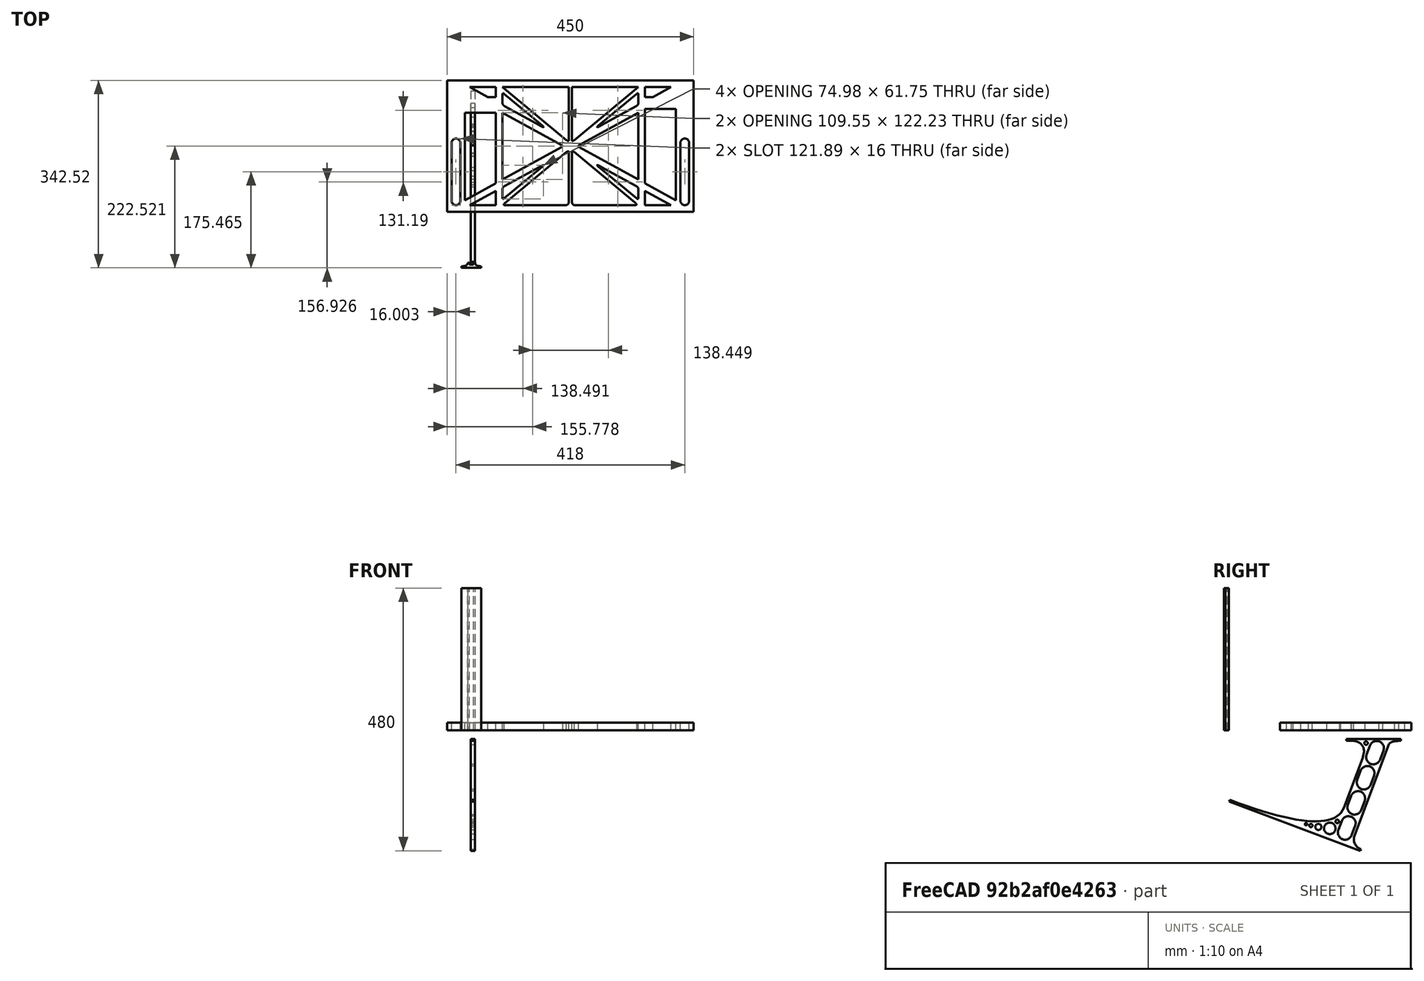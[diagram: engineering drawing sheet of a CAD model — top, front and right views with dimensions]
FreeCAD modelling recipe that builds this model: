
FCSTD DOCUMENT  (FreeCAD 0.19R0.19.2)
Label: laptopStand082
License: All rights reserved
LicenseURL: http://en.wikipedia.org/wiki/All_rights_reserved
objects: Sketcher::SketchObject×3, Part::Extrusion×3
note: 6 computed .brp shape members not serialized (recipe doc carries the construction recipe); baked Part::Feature solids carry a one-line shape summary decoded from their .brp

FEATURE [Sketcher::SketchObject] Sketch
  FullyConstrained = false
  sketch-geometry (204):
    g0: LineSegment StartX=-10.9272 StartY=-82.7794 StartZ=0 EndX=46.0728 EndY=-51.4823 EndZ=0
    g1: LineSegment StartX=366.073 StartY=-91.7794 StartZ=0 EndX=318.073 EndY=-65.424 EndZ=0
    g2: LineSegment StartX=-10.9272 StartY=77.3346 StartZ=0 EndX=-10.9272 EndY=-82.7794 EndZ=0
    g3: LineSegment StartX=375.073 StartY=-82.7794 StartZ=0 EndX=375.073 EndY=83.9235 EndZ=0
    g4: LineSegment StartX=-1.92719 StartY=-91.7794 StartZ=0 EndX=46.0728 EndY=-91.7794 EndZ=0
    g5: LineSegment StartX=318.073 StartY=124.221 StartZ=0 EndX=366.073 EndY=124.221 EndZ=0
    g6: LineSegment StartX=306.073 StartY=124.221 StartZ=0 EndX=189.124 EndY=27.0628 EndZ=0
    g7: LineSegment StartX=175.022 StartY=27.0628 StartZ=0 EndX=58.0728 EndY=124.221 EndZ=0
    g8: LineSegment StartX=306.073 StartY=77.3346 StartZ=0 EndX=306.073 EndY=-44.8935 EndZ=0
    g9: LineSegment StartX=318.073 StartY=83.9235 StartZ=0 EndX=318.073 EndY=-51.4823 EndZ=0
    g10: LineSegment StartX=318.073 StartY=-51.4823 StartZ=0 EndX=375.073 EndY=-82.7794 EndZ=0
    g11: LineSegment StartX=318.073 StartY=-65.424 StartZ=0 EndX=318.073 EndY=-91.7794 EndZ=0
    g12: LineSegment StartX=318.073 StartY=-91.7794 StartZ=0 EndX=366.073 EndY=-91.7794 EndZ=0
    g13: LineSegment StartX=58.0728 StartY=-44.8935 StartZ=0 EndX=58.0728 EndY=77.3346 EndZ=0
    g14: LineSegment StartX=46.0728 StartY=-65.424 StartZ=0 EndX=-1.92719 EndY=-91.7794 EndZ=0
    g15: LineSegment StartX=46.0728 StartY=-65.424 StartZ=0 EndX=46.0728 EndY=-91.7794 EndZ=0
    g16: LineSegment StartX=46.0728 StartY=77.3346 StartZ=0 EndX=46.0728 EndY=-51.4823 EndZ=0
    g17: LineSegment StartX=-42.9272 StartY=136.221 StartZ=0 EndX=-42.9272 EndY=-103.779 EndZ=0
    g18: LineSegment StartX=407.073 StartY=136.221 StartZ=0 EndX=407.073 EndY=-103.779 EndZ=0
    g19: LineSegment StartX=179.022 StartY=27.0628 StartZ=0 EndX=179.022 EndY=124.221 EndZ=0
    g20: LineSegment StartX=185.124 StartY=27.0628 StartZ=0 EndX=185.124 EndY=124.221 EndZ=0
    g21: ArcOfCircle CenterX=-26.9272 CenterY=22.1087 CenterZ=0 NormalX=0 NormalY=0 NormalZ=1 AngleXU=0 Radius=8 StartAngle=1e-16 EndAngle=3.14159
    g22: ArcOfCircle CenterX=-26.9272 CenterY=-83.7794 CenterZ=0 NormalX=0 NormalY=0 NormalZ=1 AngleXU=0 Radius=8 StartAngle=3.14159 EndAngle=6.28319
    g23: LineSegment StartX=-34.9272 StartY=22.1087 StartZ=0 EndX=-34.9272 EndY=-83.7794 EndZ=0
    g24: LineSegment StartX=-18.9272 StartY=22.1087 StartZ=0 EndX=-18.9272 EndY=-83.7794 EndZ=0
    g25: LineSegment StartX=306.073 StartY=124.221 StartZ=0 EndX=185.124 EndY=124.221 EndZ=0
    g26: LineSegment StartX=179.022 StartY=124.221 StartZ=0 EndX=58.0728 EndY=124.221 EndZ=0
    g27: ArcOfCircle CenterX=391.073 CenterY=22.1087 CenterZ=0 NormalX=0 NormalY=0 NormalZ=1 AngleXU=0 Radius=8 StartAngle=-4.4e-15 EndAngle=3.14159
    g28: LineSegment StartX=399.073 StartY=22.1087 StartZ=0 EndX=399.073 EndY=-83.7794 EndZ=0
    g29: LineSegment StartX=383.073 StartY=22.1087 StartZ=0 EndX=383.073 EndY=-83.7794 EndZ=0
    g30: ArcOfCircle CenterX=391.073 CenterY=-83.7794 CenterZ=0 NormalX=0 NormalY=0 NormalZ=1 AngleXU=0 Radius=8 StartAngle=3.14159 EndAngle=6.28319
    g31: Circle CenterX=175.022 CenterY=27.0628 CenterZ=0 NormalX=0 NormalY=0 NormalZ=1 AngleXU=0 Radius=1
    g32: Circle CenterX=179.022 CenterY=24.8665 CenterZ=0 NormalX=0 NormalY=0 NormalZ=1 AngleXU=0 Radius=1
    g33: Circle CenterX=179.022 CenterY=27.0628 CenterZ=0 NormalX=0 NormalY=0 NormalZ=1 AngleXU=0 Radius=1
    g34: BSplineCurve PolesCount=3 KnotsCount=2 Degree=2 IsPeriodic=0
    g35: GeomPoint X=175.022 Y=27.0628 Z=0
    g36: GeomPoint X=179.022 Y=27.0628 Z=0
    g37: Circle CenterX=189.124 CenterY=27.0628 CenterZ=0 NormalX=0 NormalY=0 NormalZ=1 AngleXU=0 Radius=1
    g38: Circle CenterX=185.124 CenterY=24.8665 CenterZ=0 NormalX=0 NormalY=0 NormalZ=1 AngleXU=0 Radius=1
    g39: Circle CenterX=185.124 CenterY=27.0628 CenterZ=0 NormalX=0 NormalY=0 NormalZ=1 AngleXU=0 Radius=1
    g40: BSplineCurve PolesCount=3 KnotsCount=2 Degree=2 IsPeriodic=0
    g41: GeomPoint X=189.124 Y=27.0628 Z=0
    g42: GeomPoint X=185.124 Y=27.0628 Z=0
    g43: Circle CenterX=175.022 CenterY=5.37834 CenterZ=0 NormalX=0 NormalY=0 NormalZ=1 AngleXU=0 Radius=1
    g44: Circle CenterX=179.022 CenterY=7.57463 CenterZ=0 NormalX=0 NormalY=0 NormalZ=1 AngleXU=0 Radius=1
    g45: Circle CenterX=179.022 CenterY=5.34704 CenterZ=0 NormalX=0 NormalY=0 NormalZ=1 AngleXU=0 Radius=1
    g46: BSplineCurve PolesCount=3 KnotsCount=2 Degree=2 IsPeriodic=0
    g47: GeomPoint X=175.022 Y=5.37834 Z=0
    g48: GeomPoint X=179.022 Y=5.34704 Z=0
    g49: Circle CenterX=189.124 CenterY=5.37834 CenterZ=0 NormalX=0 NormalY=0 NormalZ=1 AngleXU=0 Radius=1
    g50: Circle CenterX=185.124 CenterY=7.57463 CenterZ=0 NormalX=0 NormalY=0 NormalZ=1 AngleXU=0 Radius=1
    g51: Circle CenterX=185.124 CenterY=5.34704 CenterZ=0 NormalX=0 NormalY=0 NormalZ=1 AngleXU=0 Radius=1
    g52: BSplineCurve PolesCount=3 KnotsCount=2 Degree=2 IsPeriodic=0
    g53: GeomPoint X=189.124 Y=5.37834 Z=0
    g54: GeomPoint X=185.124 Y=5.34704 Z=0
    g55: Circle CenterX=165.871 CenterY=18.1458 CenterZ=0 NormalX=0 NormalY=0 NormalZ=1 AngleXU=0 Radius=1
    g56: Circle CenterX=169.377 CenterY=16.2206 CenterZ=0 NormalX=0 NormalY=0 NormalZ=1 AngleXU=0 Radius=1
    g57: Circle CenterX=165.871 CenterY=14.2954 CenterZ=0 NormalX=0 NormalY=0 NormalZ=1 AngleXU=0 Radius=1
    g58: BSplineCurve PolesCount=3 KnotsCount=2 Degree=2 IsPeriodic=0
    g59: GeomPoint X=165.871 Y=18.1458 Z=0
    g60: GeomPoint X=165.871 Y=14.2954 Z=0
    g61: Circle CenterX=198.275 CenterY=18.1458 CenterZ=0 NormalX=0 NormalY=0 NormalZ=1 AngleXU=0 Radius=1
    g62: Circle CenterX=194.768 CenterY=16.2206 CenterZ=0 NormalX=0 NormalY=0 NormalZ=1 AngleXU=0 Radius=1
    g63: Circle CenterX=198.275 CenterY=14.2954 CenterZ=0 NormalX=0 NormalY=0 NormalZ=1 AngleXU=0 Radius=1
    g64: BSplineCurve PolesCount=3 KnotsCount=2 Degree=2 IsPeriodic=0
    g65: GeomPoint X=198.275 Y=18.1458 Z=0
    g66: GeomPoint X=198.275 Y=14.2954 Z=0
    g67: LineSegment StartX=165.871 StartY=18.1458 StartZ=0 EndX=58.0728 EndY=77.3346 EndZ=0
    g68: LineSegment StartX=58.0728 StartY=-44.8935 StartZ=0 EndX=165.871 EndY=14.2954 EndZ=0
    g69: LineSegment StartX=198.275 StartY=18.1458 StartZ=0 EndX=306.073 EndY=77.3346 EndZ=0
    g70: LineSegment StartX=198.275 StartY=14.2954 StartZ=0 EndX=306.073 EndY=-44.8935 EndZ=0
    g71: LineSegment StartX=407.073 StartY=-103.779 StartZ=0 EndX=-42.9272 EndY=-103.779 EndZ=0
    g72: LineSegment StartX=407.073 StartY=136.221 StartZ=0 EndX=-42.9272 EndY=136.221 EndZ=0
    g73: LineSegment StartX=46.0728 StartY=77.3346 StartZ=0 EndX=-10.9272 EndY=77.3346 EndZ=0
    g74: LineSegment StartX=46.0728 StartY=105.865 StartZ=0 EndX=31.5028 EndY=105.865 EndZ=0
    g75: LineSegment StartX=46.0728 StartY=124.221 StartZ=0 EndX=46.0728 EndY=105.865 EndZ=0
    g76: LineSegment StartX=-1.92719 StartY=124.221 StartZ=0 EndX=31.5028 EndY=105.865 EndZ=0
    g77: LineSegment StartX=46.0728 StartY=124.221 StartZ=0 EndX=-1.92719 EndY=124.221 EndZ=0
    g78: LineSegment StartX=318.073 StartY=83.9235 StartZ=0 EndX=375.073 EndY=83.9235 EndZ=0
    g79: LineSegment StartX=318.073 StartY=105.865 StartZ=0 EndX=332.643 EndY=105.865 EndZ=0
    g80: LineSegment StartX=332.643 StartY=105.865 StartZ=0 EndX=366.073 EndY=124.221 EndZ=0
    g81: LineSegment StartX=318.073 StartY=124.221 StartZ=0 EndX=318.073 EndY=105.865 EndZ=0
    g82: Circle CenterX=125.607 CenterY=54.1951 CenterZ=0 NormalX=0 NormalY=0 NormalZ=1 AngleXU=0 Radius=1
    g83: Circle CenterX=139.632 CenterY=46.4944 CenterZ=0 NormalX=0 NormalY=0 NormalZ=1 AngleXU=0 Radius=1
    g84: Circle CenterX=127.326 CenterY=56.7187 CenterZ=0 NormalX=0 NormalY=0 NormalZ=1 AngleXU=0 Radius=1
    g85: BSplineCurve PolesCount=3 KnotsCount=2 Degree=2 IsPeriodic=0
    g86: GeomPoint X=125.607 Y=54.1951 Z=0
    g87: GeomPoint X=127.326 Y=56.7187 Z=0
    g88: Circle CenterX=236.821 CenterY=56.7187 CenterZ=0 NormalX=0 NormalY=0 NormalZ=1 AngleXU=0 Radius=1
    g89: Circle CenterX=224.513 CenterY=46.4944 CenterZ=0 NormalX=0 NormalY=0 NormalZ=1 AngleXU=0 Radius=1
    g90: Circle CenterX=238.538 CenterY=54.1951 CenterZ=0 NormalX=0 NormalY=0 NormalZ=1 AngleXU=0 Radius=1
    g91: BSplineCurve PolesCount=3 KnotsCount=2 Degree=2 IsPeriodic=0
    g92: GeomPoint X=236.821 Y=56.7187 Z=0
    g93: GeomPoint X=238.538 Y=54.1951 Z=0
    g94: Circle CenterX=238.538 CenterY=-21.7539 CenterZ=0 NormalX=0 NormalY=0 NormalZ=1 AngleXU=0 Radius=1
    g95: Circle CenterX=224.513 CenterY=-14.0532 CenterZ=0 NormalX=0 NormalY=0 NormalZ=1 AngleXU=0 Radius=1
    g96: Circle CenterX=236.821 CenterY=-24.2775 CenterZ=0 NormalX=0 NormalY=0 NormalZ=1 AngleXU=0 Radius=1
    g97: BSplineCurve PolesCount=3 KnotsCount=2 Degree=2 IsPeriodic=0
    g98: GeomPoint X=238.538 Y=-21.7539 Z=0
    g99: GeomPoint X=236.821 Y=-24.2775 Z=0
    g100: Circle CenterX=125.607 CenterY=-21.7539 CenterZ=0 NormalX=0 NormalY=0 NormalZ=1 AngleXU=0 Radius=1
    g101: Circle CenterX=139.632 CenterY=-14.0532 CenterZ=0 NormalX=0 NormalY=0 NormalZ=1 AngleXU=0 Radius=1
    g102: Circle CenterX=127.325 CenterY=-24.2775 CenterZ=0 NormalX=0 NormalY=0 NormalZ=1 AngleXU=0 Radius=1
    g103: BSplineCurve PolesCount=3 KnotsCount=2 Degree=2 IsPeriodic=0
    g104: GeomPoint X=125.607 Y=-21.7539 Z=0
    g105: GeomPoint X=127.325 Y=-24.2775 Z=0
    g106: Circle CenterX=302.996 CenterY=111.695 CenterZ=0 NormalX=0 NormalY=0 NormalZ=1 AngleXU=0 Radius=1
    g107: Circle CenterX=306.073 CenterY=114.251 CenterZ=0 NormalX=0 NormalY=0 NormalZ=1 AngleXU=0 Radius=1
    g108: Circle CenterX=306.073 CenterY=110.251 CenterZ=0 NormalX=0 NormalY=0 NormalZ=1 AngleXU=0 Radius=1
    g109: BSplineCurve PolesCount=3 KnotsCount=2 Degree=2 IsPeriodic=0
    g110: GeomPoint X=302.996 Y=111.695 Z=0
    g111: GeomPoint X=306.073 Y=110.251 Z=0
    g112: Circle CenterX=306.073 CenterY=95.2763 CenterZ=0 NormalX=0 NormalY=0 NormalZ=1 AngleXU=0 Radius=1
    g113: Circle CenterX=306.073 CenterY=91.2763 CenterZ=0 NormalX=0 NormalY=0 NormalZ=1 AngleXU=0 Radius=1
    g114: Circle CenterX=302.567 CenterY=89.3511 CenterZ=0 NormalX=0 NormalY=0 NormalZ=1 AngleXU=0 Radius=1
    g115: BSplineCurve PolesCount=3 KnotsCount=2 Degree=2 IsPeriodic=0
    g116: GeomPoint X=306.073 Y=95.2763 Z=0
    g117: GeomPoint X=302.567 Y=89.3511 Z=0
    g118: LineSegment StartX=306.073 StartY=110.251 StartZ=0 EndX=306.073 EndY=95.2763 EndZ=0
    g119: LineSegment StartX=302.996 StartY=111.695 StartZ=0 EndX=236.821 EndY=56.7187 EndZ=0
    g120: LineSegment StartX=238.538 StartY=54.1951 StartZ=0 EndX=302.567 EndY=89.3511 EndZ=0
    g121: Circle CenterX=61.1496 CenterY=111.695 CenterZ=0 NormalX=0 NormalY=0 NormalZ=1 AngleXU=0 Radius=1
    g122: Circle CenterX=58.0728 CenterY=114.251 CenterZ=0 NormalX=0 NormalY=0 NormalZ=1 AngleXU=0 Radius=1
    g123: Circle CenterX=58.0728 CenterY=110.251 CenterZ=0 NormalX=0 NormalY=0 NormalZ=1 AngleXU=0 Radius=1
    g124: BSplineCurve PolesCount=3 KnotsCount=2 Degree=2 IsPeriodic=0
    g125: GeomPoint X=61.1496 Y=111.695 Z=0
    g126: GeomPoint X=58.0728 Y=110.251 Z=0
    g127: Circle CenterX=61.5791 CenterY=89.3511 CenterZ=0 NormalX=0 NormalY=0 NormalZ=1 AngleXU=0 Radius=1
    g128: Circle CenterX=58.0728 CenterY=91.2763 CenterZ=0 NormalX=0 NormalY=0 NormalZ=1 AngleXU=0 Radius=1
    g129: Circle CenterX=58.0728 CenterY=95.2763 CenterZ=0 NormalX=0 NormalY=0 NormalZ=1 AngleXU=0 Radius=1
    g130: BSplineCurve PolesCount=3 KnotsCount=2 Degree=2 IsPeriodic=0
    g131: GeomPoint X=61.5791 Y=89.3511 Z=0
    g132: GeomPoint X=58.0728 Y=95.2763 Z=0
    g133: LineSegment StartX=58.0728 StartY=110.251 StartZ=0 EndX=58.0728 EndY=95.2763 EndZ=0
    g134: LineSegment StartX=61.1496 StartY=111.695 StartZ=0 EndX=127.326 EndY=56.7187 EndZ=0
    g135: LineSegment StartX=125.607 StartY=54.1951 StartZ=0 EndX=61.5791 EndY=89.3511 EndZ=0
    g136: Circle CenterX=61.5791 CenterY=-56.9099 CenterZ=0 NormalX=0 NormalY=0 NormalZ=1 AngleXU=0 Radius=1
    g137: Circle CenterX=58.0728 CenterY=-58.8351 CenterZ=0 NormalX=0 NormalY=0 NormalZ=1 AngleXU=0 Radius=1
    g138: Circle CenterX=58.0728 CenterY=-62.8351 CenterZ=0 NormalX=0 NormalY=0 NormalZ=1 AngleXU=0 Radius=1
    g139: BSplineCurve PolesCount=3 KnotsCount=2 Degree=2 IsPeriodic=0
    g140: GeomPoint X=61.5791 Y=-56.9099 Z=0
    g141: GeomPoint X=58.0728 Y=-62.8351 Z=0
    g142: Circle CenterX=58.0728 CenterY=-77.8102 CenterZ=0 NormalX=0 NormalY=0 NormalZ=1 AngleXU=0 Radius=1
    g143: Circle CenterX=58.0728 CenterY=-81.8102 CenterZ=0 NormalX=0 NormalY=0 NormalZ=1 AngleXU=0 Radius=1
    g144: Circle CenterX=61.1496 CenterY=-79.2541 CenterZ=0 NormalX=0 NormalY=0 NormalZ=1 AngleXU=0 Radius=1
    g145: BSplineCurve PolesCount=3 KnotsCount=2 Degree=2 IsPeriodic=0
    g146: GeomPoint X=58.0728 Y=-77.8102 Z=0
    g147: GeomPoint X=61.1496 Y=-79.2541 Z=0
    g148: LineSegment StartX=58.0728 StartY=-62.8351 StartZ=0 EndX=58.0728 EndY=-77.8102 EndZ=0
    g149: LineSegment StartX=61.1496 StartY=-79.2541 StartZ=0 EndX=127.325 EndY=-24.2775 EndZ=0
    g150: LineSegment StartX=125.607 StartY=-21.7539 StartZ=0 EndX=61.5791 EndY=-56.9099 EndZ=0
    g151: Circle CenterX=302.567 CenterY=-56.9099 CenterZ=0 NormalX=0 NormalY=0 NormalZ=1 AngleXU=0 Radius=1
    g152: Circle CenterX=306.073 CenterY=-58.8351 CenterZ=0 NormalX=0 NormalY=0 NormalZ=1 AngleXU=0 Radius=1
    g153: Circle CenterX=306.073 CenterY=-62.8351 CenterZ=0 NormalX=0 NormalY=0 NormalZ=1 AngleXU=0 Radius=1
    g154: BSplineCurve PolesCount=3 KnotsCount=2 Degree=2 IsPeriodic=0
    g155: GeomPoint X=302.567 Y=-56.9099 Z=0
    g156: GeomPoint X=306.073 Y=-62.8351 Z=0
    g157: Circle CenterX=302.996 CenterY=-79.2541 CenterZ=0 NormalX=0 NormalY=0 NormalZ=1 AngleXU=0 Radius=1
    g158: Circle CenterX=306.073 CenterY=-81.8102 CenterZ=0 NormalX=0 NormalY=0 NormalZ=1 AngleXU=0 Radius=1
    g159: Circle CenterX=306.073 CenterY=-77.8102 CenterZ=0 NormalX=0 NormalY=0 NormalZ=1 AngleXU=0 Radius=1
    g160: BSplineCurve PolesCount=3 KnotsCount=2 Degree=2 IsPeriodic=0
    g161: GeomPoint X=302.996 Y=-79.2541 Z=0
    g162: GeomPoint X=306.073 Y=-77.8102 Z=0
    g163: LineSegment StartX=306.073 StartY=-62.8351 StartZ=0 EndX=306.073 EndY=-77.8102 EndZ=0
    g164: LineSegment StartX=302.996 StartY=-79.2541 StartZ=0 EndX=236.821 EndY=-24.2775 EndZ=0
    g165: LineSegment StartX=238.538 StartY=-21.7539 StartZ=0 EndX=302.567 EndY=-56.9099 EndZ=0
    g166: Circle CenterX=61.6457 CenterY=-88.8112 CenterZ=0 NormalX=0 NormalY=0 NormalZ=1 AngleXU=0 Radius=1
    g167: Circle CenterX=58.0728 CenterY=-91.7794 CenterZ=0 NormalX=0 NormalY=0 NormalZ=1 AngleXU=0 Radius=1
    g168: Circle CenterX=63.9135 CenterY=-91.7794 CenterZ=0 NormalX=0 NormalY=0 NormalZ=1 AngleXU=0 Radius=1
    g169: BSplineCurve PolesCount=3 KnotsCount=2 Degree=2 IsPeriodic=0
    g170: GeomPoint X=61.6457 Y=-88.8112 Z=0
    g171: GeomPoint X=63.9135 Y=-91.7794 Z=0
    g172: Circle CenterX=179.022 CenterY=-85.8163 CenterZ=0 NormalX=0 NormalY=0 NormalZ=1 AngleXU=0 Radius=1
    g173: Circle CenterX=179.022 CenterY=-91.7794 CenterZ=0 NormalX=0 NormalY=0 NormalZ=1 AngleXU=0 Radius=1
    g174: Circle CenterX=171.895 CenterY=-91.7794 CenterZ=0 NormalX=0 NormalY=0 NormalZ=1 AngleXU=0 Radius=1
    g175: BSplineCurve PolesCount=3 KnotsCount=2 Degree=2 IsPeriodic=0
    g176: GeomPoint X=179.022 Y=-85.8163 Z=0
    g177: GeomPoint X=171.895 Y=-91.7794 Z=0
    g178: Circle CenterX=185.124 CenterY=-86.2028 CenterZ=0 NormalX=0 NormalY=0 NormalZ=1 AngleXU=0 Radius=1
    g179: Circle CenterX=185.124 CenterY=-91.7794 CenterZ=0 NormalX=0 NormalY=0 NormalZ=1 AngleXU=0 Radius=1
    g180: Circle CenterX=191.747 CenterY=-91.7794 CenterZ=0 NormalX=0 NormalY=0 NormalZ=1 AngleXU=0 Radius=1
    g181: BSplineCurve PolesCount=3 KnotsCount=2 Degree=2 IsPeriodic=0
    g182: GeomPoint X=185.124 Y=-86.2028 Z=0
    g183: GeomPoint X=191.747 Y=-91.7794 Z=0
    g184: Circle CenterX=299.888 CenterY=-86.6413 CenterZ=0 NormalX=0 NormalY=0 NormalZ=1 AngleXU=0 Radius=1
    g185: Circle CenterX=306.073 CenterY=-91.7794 CenterZ=0 NormalX=0 NormalY=0 NormalZ=1 AngleXU=0 Radius=1
    g186: Circle CenterX=298.776 CenterY=-91.7794 CenterZ=0 NormalX=0 NormalY=0 NormalZ=1 AngleXU=0 Radius=1
    g187: BSplineCurve PolesCount=3 KnotsCount=2 Degree=2 IsPeriodic=0
    g188: GeomPoint X=299.888 Y=-86.6413 Z=0
    g189: GeomPoint X=298.776 Y=-91.7794 Z=0
    g190: LineSegment StartX=189.124 StartY=5.37834 StartZ=0 EndX=299.888 EndY=-86.6413 EndZ=0
    g191: LineSegment StartX=298.776 StartY=-91.7794 StartZ=0 EndX=191.747 EndY=-91.7794 EndZ=0
    g192: LineSegment StartX=185.124 StartY=-86.2028 StartZ=0 EndX=185.124 EndY=5.34704 EndZ=0
    g193: LineSegment StartX=179.022 StartY=5.34704 StartZ=0 EndX=179.022 EndY=-85.8163 EndZ=0
    g194: LineSegment StartX=171.895 StartY=-91.7794 StartZ=0 EndX=63.9135 EndY=-91.7794 EndZ=0
    g195: LineSegment StartX=61.6457 StartY=-88.8112 StartZ=0 EndX=175.022 EndY=5.37834 EndZ=0
    g196: LineSegment StartX=306.216 StartY=121.907 StartZ=0 EndX=303.139 EndY=119.351 EndZ=0
    g197: LineSegment StartX=302.162 StartY=125.431 StartZ=0 EndX=298.162 EndY=125.431 EndZ=0
    g198: LineSegment StartX=188.167 StartY=125.477 StartZ=0 EndX=192.167 EndY=125.477 EndZ=0
    g199: LineSegment StartX=184.375 StartY=120.182 StartZ=0 EndX=184.375 EndY=116.182 EndZ=0
    g200: LineSegment StartX=179.954 StartY=121.298 StartZ=0 EndX=179.954 EndY=117.298 EndZ=0
    g201: LineSegment StartX=177.401 StartY=125.133 StartZ=0 EndX=173.401 EndY=125.133 EndZ=0
    g202: LineSegment StartX=60.572 StartY=125.179 StartZ=0 EndX=64.572 EndY=125.179 EndZ=0
    g203: LineSegment StartX=60.0631 StartY=120.993 StartZ=0 EndX=63.1399 EndY=118.437 EndZ=0
  constraints (355):
    c: Horizontal(g4)
    c: Horizontal(g5)
    c: Coincident(g9,g10)
    c: Coincident(g11,g1)
    c: Tangent(g9,g11)
    c: Coincident(g15,g14)
    c: Coincident(g0,g16)
    c: Block(g7)
    c: Block(g6)
    c: Block(g10)
    c: Block(g3)
    c: Block(g1)
    c: Block(g11)
    c: Block(g15)
    c: Block(g14)
    c: Block(g0)
    c: Block(g2)
    c: Block(g8)
    c: Block(g5)
    c: Block(g12)
    c: Block(g4)
    c: Vertical(g17)
    c: Vertical(g18)
    c: Block(g18)
    c: Block(g17)
    c: Vertical(g19)
    c: Vertical(g20)
    c: Block(g19)
    c: Block(g20)
    c: Tangent(g21,g24) = 1.5708
    c: Tangent(g21,g23) = -1.5708
    c: Tangent(g23,g22) = -1.5708
    c: Tangent(g24,g22) = 1.5708
    c: Vertical(g23)
    c: Equal(g21,g22)
    c: Block(g24)
    c: Block(g23)
    c: Coincident(g25,g6)
    c: Coincident(g25,g20)
    c: Horizontal(g25)
    c: Coincident(g26,g19)
    c: Coincident(g26,g7)
    c: Horizontal(g26)
    c: Tangent(g27,g28) = 1.5708
    c: Tangent(g28,g30) = 1.5708
    c: Equal(g27,g30)
    c: Coincident(g29,g27)
    c: Coincident(g29,g30)
    c: Block(g28)
    c: Block(g29)
    c: Coincident(g34,g7)
    c: Weight(g31) = 1
    c: Equal(g31,g32)
    c: Equal(g31,g33)
    c: Coincident(g34,g19)
    c: InternalAlignment(g31,g34)
    c: InternalAlignment(g32,g34)
    c: InternalAlignment(g33,g34)
    c: InternalAlignment(g35,g34)
    c: InternalAlignment(g36,g34)
    c: Coincident(g40,g6)
    c: Weight(g37) = 1
    c: Equal(g37,g38)
    c: Equal(g37,g39)
    c: Coincident(g40,g20)
    c: InternalAlignment(g37,g40)
    c: InternalAlignment(g38,g40)
    c: InternalAlignment(g39,g40)
    c: InternalAlignment(g41,g40)
    c: InternalAlignment(g42,g40)
    c: Block(g40)
    c: Block(g34)
    c: Weight(g43) = 1
    c: Equal(g43,g44)
    c: Equal(g43,g45)
    c: InternalAlignment(g43,g46)
    c: InternalAlignment(g44,g46)
    c: InternalAlignment(g45,g46)
    c: InternalAlignment(g47,g46)
    c: InternalAlignment(g48,g46)
    c: Weight(g49) = 1
    c: Equal(g49,g50)
    c: Equal(g49,g51)
    c: InternalAlignment(g49,g52)
    c: InternalAlignment(g50,g52)
    c: InternalAlignment(g51,g52)
    c: InternalAlignment(g53,g52)
    c: InternalAlignment(g54,g52)
    c: Block(g52)
    c: Block(g46)
    c: Weight(g55) = 1
    c: Equal(g55,g56)
    c: Equal(g55,g57)
    c: InternalAlignment(g55,g58)
    c: InternalAlignment(g56,g58)
    c: InternalAlignment(g57,g58)
    c: InternalAlignment(g59,g58)
    c: InternalAlignment(g60,g58)
    c: Weight(g61) = 1
    c: Equal(g61,g62)
    c: Equal(g61,g63)
    c: InternalAlignment(g61,g64)
    c: InternalAlignment(g62,g64)
    c: InternalAlignment(g63,g64)
    c: InternalAlignment(g65,g64)
    c: InternalAlignment(g66,g64)
    c: Block(g58)
    c: Block(g64)
    c: Coincident(g67,g58)
    c: Coincident(g67,g13)
    c: Coincident(g68,g13)
    c: Coincident(g68,g58)
    c: Coincident(g69,g64)
    c: Coincident(g69,g8)
    c: Coincident(g70,g64)
    c: Coincident(g70,g8)
    c: Block(g13)
    c: Coincident(g71,g18)
    c: Coincident(g71,g17)
    c: Horizontal(g71)
    c: Distance(g71) = 450
    c: Coincident(g72,g18)
    c: Coincident(g72,g17)
    c: Horizontal(g72)
    c: Horizontal(g73)
    c: Coincident(g16,g73)
    c: Horizontal(g74)
    c: Vertical(g75)
    c: Block(g75)
    c: Block(g74)
    c: Block(g73)
    c: Distance(g75) = 18.3554
    c: Coincident(g77,g75)
    c: Coincident(g77,g76)
    c: Horizontal(g77)
    c: Block(g77)
    c: Block(g76)
    c: Coincident(g74,g76)
    c: Coincident(g2,g73)
    c: Coincident(g78,g9)
    c: Horizontal(g78)
    c: Horizontal(g79)
    c: Block(g78)
    c: Coincident(g80,g5)
    c: Coincident(g81,g5)
    c: Coincident(g81,g79)
    c: Vertical(g81)
    c: Block(g81)
    c: Coincident(g79,g80)
    c: Block(g80)
    c: Coincident(g3,g78)
    c: Weight(g82) = 1
    c: Equal(g82,g83)
    c: Equal(g82,g84)
    c: InternalAlignment(g82,g85)
    c: InternalAlignment(g83,g85)
    c: InternalAlignment(g84,g85)
    c: InternalAlignment(g86,g85)
    c: InternalAlignment(g87,g85)
    c: Block(g85)
    c: Weight(g88) = 1
    c: Equal(g88,g89)
    c: Equal(g88,g90)
    c: InternalAlignment(g88,g91)
    c: InternalAlignment(g89,g91)
    c: InternalAlignment(g90,g91)
    c: InternalAlignment(g92,g91)
    c: InternalAlignment(g93,g91)
    c: Block(g91)
    c: Weight(g94) = 1
    c: Equal(g94,g95)
    c: Equal(g94,g96)
    c: InternalAlignment(g94,g97)
    c: InternalAlignment(g95,g97)
    c: InternalAlignment(g96,g97)
    c: InternalAlignment(g98,g97)
    c: InternalAlignment(g99,g97)
    c: Block(g97)
    c: Weight(g100) = 1
    c: Equal(g100,g101)
    c: Equal(g100,g102)
    c: InternalAlignment(g100,g103)
    c: InternalAlignment(g101,g103)
    c: InternalAlignment(g102,g103)
    c: InternalAlignment(g104,g103)
    c: InternalAlignment(g105,g103)
    c: Block(g103)
    c: Weight(g106) = 1
    c: Equal(g106,g107)
    c: Equal(g106,g108)
    c: InternalAlignment(g106,g109)
    c: InternalAlignment(g107,g109)
    c: InternalAlignment(g108,g109)
    c: InternalAlignment(g110,g109)
    c: InternalAlignment(g111,g109)
    c: Weight(g112) = 1
    c: Equal(g112,g113)
    c: Equal(g112,g114)
    c: InternalAlignment(g112,g115)
    c: InternalAlignment(g113,g115)
    c: InternalAlignment(g114,g115)
    c: InternalAlignment(g116,g115)
    c: InternalAlignment(g117,g115)
    c: Block(g109)
    c: Block(g115)
    c: Coincident(g118,g109)
    c: Coincident(g118,g115)
    c: Vertical(g118)
    c: Coincident(g119,g109)
    c: Coincident(g119,g91)
    c: Coincident(g120,g91)
    c: Coincident(g120,g115)
    c: Weight(g121) = 1
    c: Equal(g121,g122)
    c: Equal(g121,g123)
    c: InternalAlignment(g121,g124)
    c: InternalAlignment(g122,g124)
    c: InternalAlignment(g123,g124)
    c: InternalAlignment(g125,g124)
    c: InternalAlignment(g126,g124)
    c: Weight(g127) = 1
    c: Equal(g127,g128)
    c: Equal(g127,g129)
    c: InternalAlignment(g127,g130)
    c: InternalAlignment(g128,g130)
    c: InternalAlignment(g129,g130)
    c: InternalAlignment(g131,g130)
    c: InternalAlignment(g132,g130)
    c: Block(g124)
    c: Block(g130)
    c: Coincident(g133,g124)
    c: Coincident(g133,g130)
    c: Vertical(g133)
    c: Coincident(g134,g124)
    c: Coincident(g134,g85)
    c: Coincident(g135,g85)
    c: Coincident(g135,g130)
    c: Weight(g136) = 1
    c: Equal(g136,g137)
    c: Equal(g136,g138)
    c: InternalAlignment(g136,g139)
    c: InternalAlignment(g137,g139)
    c: InternalAlignment(g138,g139)
    c: InternalAlignment(g140,g139)
    c: InternalAlignment(g141,g139)
    c: Weight(g142) = 1
    c: Equal(g142,g143)
    c: Equal(g142,g144)
    c: InternalAlignment(g142,g145)
    c: InternalAlignment(g143,g145)
    c: InternalAlignment(g144,g145)
    c: InternalAlignment(g146,g145)
    c: InternalAlignment(g147,g145)
    c: Block(g139)
    c: Block(g145)
    c: Coincident(g148,g139)
    c: Coincident(g148,g145)
    c: Vertical(g148)
    c: Coincident(g149,g145)
    c: Coincident(g149,g103)
    c: Coincident(g150,g103)
    c: Coincident(g150,g139)
    c: Weight(g151) = 1
    c: Equal(g151,g152)
    c: Equal(g151,g153)
    c: InternalAlignment(g151,g154)
    c: InternalAlignment(g152,g154)
    c: InternalAlignment(g153,g154)
    c: InternalAlignment(g155,g154)
    c: InternalAlignment(g156,g154)
    c: Weight(g157) = 1
    c: Equal(g157,g158)
    c: Equal(g157,g159)
    c: InternalAlignment(g157,g160)
    c: InternalAlignment(g158,g160)
    c: InternalAlignment(g159,g160)
    c: InternalAlignment(g161,g160)
    c: InternalAlignment(g162,g160)
    c: Block(g154)
    c: Block(g160)
    c: Coincident(g163,g154)
    c: Coincident(g163,g160)
    c: Vertical(g163)
    c: Coincident(g164,g160)
    c: Coincident(g164,g97)
    c: Coincident(g165,g97)
    c: Coincident(g165,g154)
    c: Weight(g166) = 1
    c: Equal(g166,g167)
    c: Equal(g166,g168)
    c: InternalAlignment(g166,g169)
    c: InternalAlignment(g167,g169)
    c: InternalAlignment(g168,g169)
    c: InternalAlignment(g170,g169)
    c: InternalAlignment(g171,g169)
    c: Weight(g172) = 1
    c: Equal(g172,g173)
    c: Equal(g172,g174)
    c: InternalAlignment(g172,g175)
    c: InternalAlignment(g173,g175)
    c: InternalAlignment(g174,g175)
    c: InternalAlignment(g176,g175)
    c: InternalAlignment(g177,g175)
    c: Weight(g178) = 1
    c: Equal(g178,g179)
    c: Equal(g178,g180)
    c: InternalAlignment(g178,g181)
    c: InternalAlignment(g179,g181)
    c: InternalAlignment(g180,g181)
    c: InternalAlignment(g182,g181)
    c: InternalAlignment(g183,g181)
    c: Weight(g184) = 1
    c: Equal(g184,g185)
    c: Equal(g184,g186)
    c: InternalAlignment(g184,g187)
    c: InternalAlignment(g185,g187)
    c: InternalAlignment(g186,g187)
    c: InternalAlignment(g188,g187)
    c: InternalAlignment(g189,g187)
    c: Block(g187)
    c: Block(g181)
    c: Block(g175)
    c: Block(g169)
    c: Coincident(g190,g52)
    c: Coincident(g190,g187)
    c: Coincident(g191,g187)
    c: Coincident(g191,g181)
    c: Horizontal(g191)
    c: Coincident(g192,g181)
    c: Coincident(g192,g52)
    c: Vertical(g192)
    c: Coincident(g193,g46)
    c: Coincident(g193,g175)
    c: Vertical(g193)
    c: Coincident(g194,g175)
    c: Coincident(g194,g169)
    c: Horizontal(g194)
    c: Coincident(g195,g169)
    c: Coincident(g195,g46)
    c: Horizontal(g197)
    c: Horizontal(g198)
    c: Vertical(g199)
    c: Vertical(g200)
    c: Horizontal(g201)
    c: Horizontal(g202)
    c: Parallel(g203,g7)
    c: Parallel(g196,g6)
    c: Distance(g196) = 4
    c: Distance(g197) = 4
    c: Distance(g198) = 4
    c: Distance(g199) = 4
    c: Distance(g200) = 4
    c: Distance(g201) = 4
    c: Distance(g202) = 4
    c: Distance(g203) = 4
FEATURE [Sketcher::SketchObject] Sketch001
  FullyConstrained = true
  MapMode = 4
  Placement = pos=(0,0,0) rot=(0.57735,0.57735,0.57735;2.0944rad)
  Support = -> [Sketch]
  sketch-geometry (46):
    g0: BSplineCurve PolesCount=3 KnotsCount=2 Degree=2 IsPeriodic=0
    g1: ArcOfCircle CenterX=73.1223 CenterY=-32.291 CenterZ=0 NormalX=0 NormalY=0 NormalZ=1 AngleXU=0 Radius=13 StartAngle=5.92268 EndAngle=9.06428
    g2: ArcOfCircle CenterX=66.7816 CenterY=-49.1439 CenterZ=0 NormalX=0 NormalY=0 NormalZ=1 AngleXU=0 Radius=13 StartAngle=2.78068 EndAngle=5.92131
    g3: ArcOfCircle CenterX=55.9263 CenterY=-78.1807 CenterZ=0 NormalX=0 NormalY=0 NormalZ=1 AngleXU=0 Radius=13 StartAngle=5.92268 EndAngle=9.06428
    g4: ArcOfCircle CenterX=49.5884 CenterY=-95.0342 CenterZ=0 NormalX=0 NormalY=0 NormalZ=1 AngleXU=0 Radius=13 StartAngle=2.78068 EndAngle=5.92131
    g5: ArcOfCircle CenterX=38.7206 CenterY=-124.067 CenterZ=0 NormalX=0 NormalY=0 NormalZ=1 AngleXU=0 Radius=13 StartAngle=5.92268 EndAngle=9.06428
    g6: ArcOfCircle CenterX=32.3875 CenterY=-140.92 CenterZ=0 NormalX=0 NormalY=0 NormalZ=1 AngleXU=0 Radius=13 StartAngle=2.78068 EndAngle=5.92131
    g7: ArcOfCircle CenterX=21.4715 CenterY=-169.934 CenterZ=0 NormalX=0 NormalY=0 NormalZ=1 AngleXU=0 Radius=13 StartAngle=5.92268 EndAngle=9.06428
    g8: ArcOfCircle CenterX=15.1336 CenterY=-186.787 CenterZ=0 NormalX=0 NormalY=0 NormalZ=1 AngleXU=0 Radius=13 StartAngle=2.78068 EndAngle=5.92131
    g9-g12: Circle x4 (B-spline internal-alignment scaffolding for g13; pole/knot coordinates omitted)
    g13: BSplineCurve PolesCount=4 KnotsCount=2 Degree=3 IsPeriodic=0
    g14: GeomPoint X=28.8094 Y=-19.0875 Z=0
    g15: GeomPoint X=47.0443 Y=-50.4712 Z=0
    g16: Circle CenterX=53.5586 CenterY=-23.2695 CenterZ=0 NormalX=0 NormalY=0 NormalZ=1 AngleXU=0 Radius=3.24518
    g17: Circle CenterX=-195.441 CenterY=-127.082 CenterZ=0 NormalX=0 NormalY=0 NormalZ=1 AngleXU=0 Radius=1
    g18: Circle CenterX=-8.24091 CenterY=-197.481 CenterZ=0 NormalX=0 NormalY=0 NormalZ=1 AngleXU=0 Radius=1
    g19: Circle CenterX=12.8789 CenterY=-141.321 CenterZ=0 NormalX=0 NormalY=0 NormalZ=1 AngleXU=0 Radius=1
    g20: BSplineCurve PolesCount=3 KnotsCount=2 Degree=2 IsPeriodic=0
    g21: GeomPoint X=-195.441 Y=-127.082 Z=0
    g22: GeomPoint X=12.8789 Y=-141.321 Z=0
    g23: Circle CenterX=-12.8016 CenterY=-179.036 CenterZ=0 NormalX=0 NormalY=0 NormalZ=1 AngleXU=0 Radius=10.5072
    g24: Circle CenterX=0.933922 CenterY=-166.43 CenterZ=0 NormalX=0 NormalY=0 NormalZ=1 AngleXU=0 Radius=3.26661
    g25: Circle CenterX=-33.5518 CenterY=-176.44 CenterZ=0 NormalX=0 NormalY=0 NormalZ=1 AngleXU=0 Radius=5.64388
    g26: Circle CenterX=-47.2366 CenterY=-173.859 CenterZ=0 NormalX=0 NormalY=0 NormalZ=1 AngleXU=0 Radius=3.01653
    g27: Circle CenterX=-56.2595 CenterY=-171.456 CenterZ=0 NormalX=0 NormalY=0 NormalZ=1 AngleXU=0 Radius=2.12826
    g28: ArcOfCircle CenterX=51.2151 CenterY=-198.473 CenterZ=0 NormalX=0 NormalY=0 NormalZ=1 AngleXU=0 Radius=20 StartAngle=2.78189 EndAngle=4.35269
    g29: LineSegment StartX=32.4951 StartY=-191.433 StartZ=0 EndX=94.6578 EndY=-26.1352 EndZ=0
    g30: LineSegment StartX=43.1192 StartY=-220.001 StartZ=0 EndX=-196.497 EndY=-129.89 EndZ=0
    g31: LineSegment StartX=43.1192 StartY=-220.001 StartZ=0 EndX=44.1752 EndY=-217.193 EndZ=0
    g32: LineSegment StartX=117.223 StartY=-19.0875 StartZ=0 EndX=117.223 EndY=-16.0875 EndZ=0
    g33: LineSegment StartX=117.223 StartY=-16.0875 StartZ=0 EndX=17.2232 EndY=-16.0875 EndZ=0
    g34: LineSegment StartX=17.2232 StartY=-16.0875 StartZ=0 EndX=17.2232 EndY=-19.0875 EndZ=0
    g35: LineSegment StartX=28.8094 StartY=-19.0875 StartZ=0 EndX=17.2232 EndY=-19.0875 EndZ=0
    g36: LineSegment StartX=47.0443 StartY=-50.4712 StartZ=0 EndX=12.8789 EndY=-141.321 EndZ=0
    g37: LineSegment StartX=-195.441 StartY=-127.082 StartZ=0 EndX=-196.497 EndY=-129.89 EndZ=0
    g38: LineSegment StartX=85.2866 StartY=-36.8766 StartZ=0 EndX=78.9396 EndY=-53.7463 EndZ=0
    g39: LineSegment StartX=60.9579 StartY=-27.7053 StartZ=0 EndX=54.6191 EndY=-44.5532 EndZ=0
    g40: LineSegment StartX=68.0907 StartY=-82.7664 StartZ=0 EndX=61.7465 EndY=-99.6365 EndZ=0
    g41: LineSegment StartX=43.7619 StartY=-73.595 StartZ=0 EndX=37.426 EndY=-90.4435 EndZ=0
    g42: LineSegment StartX=50.885 StartY=-128.652 StartZ=0 EndX=44.5456 EndY=-145.522 EndZ=0
    g43: LineSegment StartX=26.5562 StartY=-119.481 StartZ=0 EndX=20.2251 EndY=-136.329 EndZ=0
    g44: LineSegment StartX=9.3071 StartY=-165.349 StartZ=0 EndX=2.97115 EndY=-182.197 EndZ=0
    g45: LineSegment StartX=33.6358 StartY=-174.52 StartZ=0 EndX=27.2917 EndY=-191.39 EndZ=0
  constraints (71):
    c: Block(g0)
    c: Block(g1)
    c: Block(g2)
    c: Block(g4)
    c: Block(g3)
    c: Block(g6)
    c: Block(g5)
    c: Block(g8)
    c: Block(g7)
    c: Weight(g9) = 1
    c: Equal(g9,g10)
    c: Equal(g9,g11)
    c: Equal(g9,g12)
    c: InternalAlignment(g9-g12 -> g13) x4
    c: InternalAlignment(g14,g13)
    c: InternalAlignment(g15,g13)
    c: Block(g16)
    c: Weight(g17) = 1
    c: Equal(g17,g18)
    c: Equal(g17,g19)
    c: InternalAlignment(g17,g20)
    c: InternalAlignment(g18,g20)
    c: InternalAlignment(g19,g20)
    c: InternalAlignment(g21,g20)
    c: InternalAlignment(g22,g20)
    c: Block(g20)
    c: Block(g23)
    c: Block(g24)
    c: Block(g25)
    c: Block(g26)
    c: Block(g27)
    c: Block(g28)
    c: Coincident(g29,g28)
    c: Coincident(g29,g0)
    c: Block(g13)
    c: Coincident(g31,g30)
    c: Coincident(g31,g28)
    c: Block(g31)
    c: Coincident(g32,g0)
    c: Vertical(g32)
    c: Coincident(g33,g32)
    c: Horizontal(g33)
    c: Coincident(g34,g33)
    c: Vertical(g34)
    c: Block(g33)
    c: Coincident(g35,g13)
    c: Coincident(g35,g34)
    c: Horizontal(g35)
    c: Coincident(g36,g13)
    c: Coincident(g36,g20)
    c: Coincident(g37,g20)
    c: Coincident(g37,g30)
    c: Block(g30)
    c: Coincident(g38,g1)
    c: Coincident(g38,g2)
    c: Coincident(g39,g1)
    c: Coincident(g39,g2)
    c: Coincident(g40,g3)
    c: Coincident(g40,g4)
    c: Coincident(g41,g3)
    c: Coincident(g41,g4)
    c: Coincident(g42,g5)
    c: Coincident(g42,g6)
    c: Coincident(g43,g5)
    c: Coincident(g43,g6)
    c: Coincident(g44,g7)
    c: Coincident(g44,g8)
    c: Coincident(g45,g7)
    c: Coincident(g45,g8)
    c: Distance(g30) = 256
    c: Distance(g33) = 100
FEATURE [Part::Extrusion] Extrude002
  Base = -> Sketch001
  Dir = (1,0,0)
  DirMode = 2
  FaceMakerClass = Part::FaceMakerBullseye
  LengthFwd = 8
  LengthRev = 0
  Solid = true
  Symmetric = false
FEATURE [Sketcher::SketchObject] Sketch002
  FullyConstrained = true
  sketch-geometry (20):
    g0: LineSegment StartX=-2.77179 StartY=-200.304 StartZ=0 EndX=5.22821 EndY=-200.304 EndZ=0
    g1: LineSegment StartX=5.22821 StartY=-200.304 StartZ=0 EndX=5.22821 EndY=-197.304 EndZ=0
    g2: LineSegment StartX=-2.77179 StartY=-200.304 StartZ=0 EndX=-2.77179 EndY=-197.304 EndZ=0
    g3: LineSegment StartX=5.22821 StartY=-197.304 StartZ=0 EndX=8.22821 EndY=-197.304 EndZ=0
    g4: LineSegment StartX=-2.77179 StartY=-197.304 StartZ=0 EndX=-5.77179 EndY=-197.304 EndZ=0
    g5: LineSegment StartX=19.2282 StartY=-203.304 StartZ=0 EndX=19.2282 EndY=-206.304 EndZ=0
    g6: LineSegment StartX=-16.7718 StartY=-203.304 StartZ=0 EndX=-16.7718 EndY=-206.304 EndZ=0
    g7: LineSegment StartX=-16.7718 StartY=-206.304 StartZ=0 EndX=19.2282 EndY=-206.304 EndZ=0
    g8: Circle CenterX=-16.7718 CenterY=-203.304 CenterZ=0 NormalX=0 NormalY=0 NormalZ=1 AngleXU=0 Radius=1
    g9: Circle CenterX=-5.77179 CenterY=-203.304 CenterZ=0 NormalX=0 NormalY=0 NormalZ=1 AngleXU=0 Radius=1
    g10: Circle CenterX=-5.77179 CenterY=-197.304 CenterZ=0 NormalX=0 NormalY=0 NormalZ=1 AngleXU=0 Radius=1
    g11: BSplineCurve PolesCount=3 KnotsCount=2 Degree=2 IsPeriodic=0
    g12: GeomPoint X=-16.7718 Y=-203.304 Z=0
    g13: GeomPoint X=-5.77179 Y=-197.304 Z=0
    g14: Circle CenterX=19.2282 CenterY=-203.304 CenterZ=0 NormalX=0 NormalY=0 NormalZ=1 AngleXU=0 Radius=1
    g15: Circle CenterX=8.22821 CenterY=-203.304 CenterZ=0 NormalX=0 NormalY=0 NormalZ=1 AngleXU=0 Radius=1
    g16: Circle CenterX=8.22821 CenterY=-197.304 CenterZ=0 NormalX=0 NormalY=0 NormalZ=1 AngleXU=0 Radius=1
    g17: BSplineCurve PolesCount=3 KnotsCount=2 Degree=2 IsPeriodic=0
    g18: GeomPoint X=19.2282 Y=-203.304 Z=0
    g19: GeomPoint X=8.22821 Y=-197.304 Z=0
  constraints (41):
    c: Horizontal(g0)
    c: Distance(g0) = 8
    c: Coincident(g1,g0)
    c: Vertical(g1)
    c: Distance(g1) = 3
    c: Coincident(g2,g0)
    c: Vertical(g2)
    c: Distance(g2) = 3
    c: Coincident(g3,g1)
    c: Horizontal(g3)
    c: Distance(g3) = 3
    c: Coincident(g4,g2)
    c: Horizontal(g4)
    c: Distance(g4) = 3
    c: Vertical(g5)
    c: Vertical(g6)
    c: Coincident(g7,g6)
    c: Coincident(g7,g5)
    c: Weight(g8) = 1
    c: Equal(g8,g9)
    c: Equal(g8,g10)
    c: Coincident(g11,g4)
    c: InternalAlignment(g8,g11)
    c: InternalAlignment(g9,g11)
    c: InternalAlignment(g10,g11)
    c: InternalAlignment(g12,g11)
    c: InternalAlignment(g13,g11)
    c: Coincident(g17,g5)
    c: Weight(g14) = 1
    c: Equal(g14,g15)
    c: Equal(g14,g16)
    c: Coincident(g17,g3)
    c: InternalAlignment(g14,g17)
    c: InternalAlignment(g15,g17)
    c: InternalAlignment(g16,g17)
    c: InternalAlignment(g18,g17)
    c: InternalAlignment(g19,g17)
    c: Block(g7)
    c: Block(g17)
    c: Block(g11)
    c: Block(g6)
FEATURE [Part::Extrusion] Extrude003
  Base = -> Sketch002
  Dir = (0,0,1)
  DirMode = 2
  FaceMakerClass = Part::FaceMakerBullseye
  LengthFwd = 260
  LengthRev = 0
  Solid = true
  Symmetric = false
FEATURE [Part::Extrusion] Extrude
  Base = -> Sketch
  Dir = (0,0,1)
  DirMode = 2
  FaceMakerClass = Part::FaceMakerBullseye
  LengthFwd = 14
  LengthRev = 0
  Solid = true
  Symmetric = false
